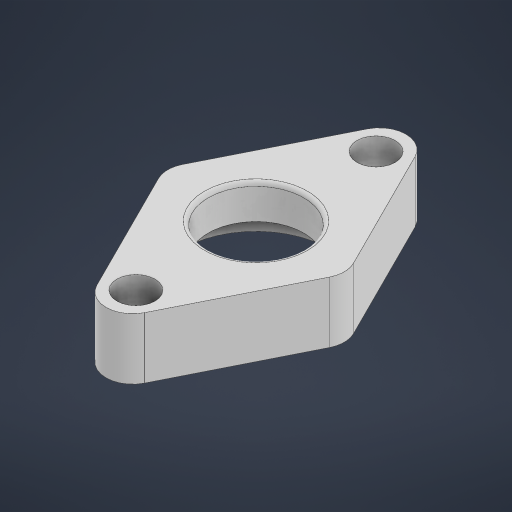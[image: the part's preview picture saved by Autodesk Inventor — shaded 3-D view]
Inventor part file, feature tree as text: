
AUTODESK INVENTOR PART (.ipt)
format: ipt  version: 2024.2 (Build 282272000, 272)  size: 211,456 bytes
history: native  units: mm
features: extrude x2, fillet x2, sketch x2
ambient origin geometry x8: Origin, YZ Plane, XZ Plane, XY Plane, X Axis, Y Axis, Z Axis, Center Point
bodies: Solid1 (feature_tree)
feature tree (6):
  extrude  "Extrusion1"  Depth=5.0mm
  fillet  "Fillet1"  Radius=5.0mm
  extrude  "Extrusion2"  Depth=15.75mm
  fillet  "Fillet2"  Radius=24.0mm
  sketch  "Sketch1"  dims[d0=12.5mm d1=5.0mm d2=5.0mm]
  sketch  "Sketch2"  dims[d3=15.75mm d4=15.75mm d5=24.0mm d6=24.0mm d7=12.0mm d8=12.0mm d9=8.0mm d10=0.0mm d11=3.5mm d12=19.25mm d13=3.5mm d14=0.0mm d15=0.5mm]
